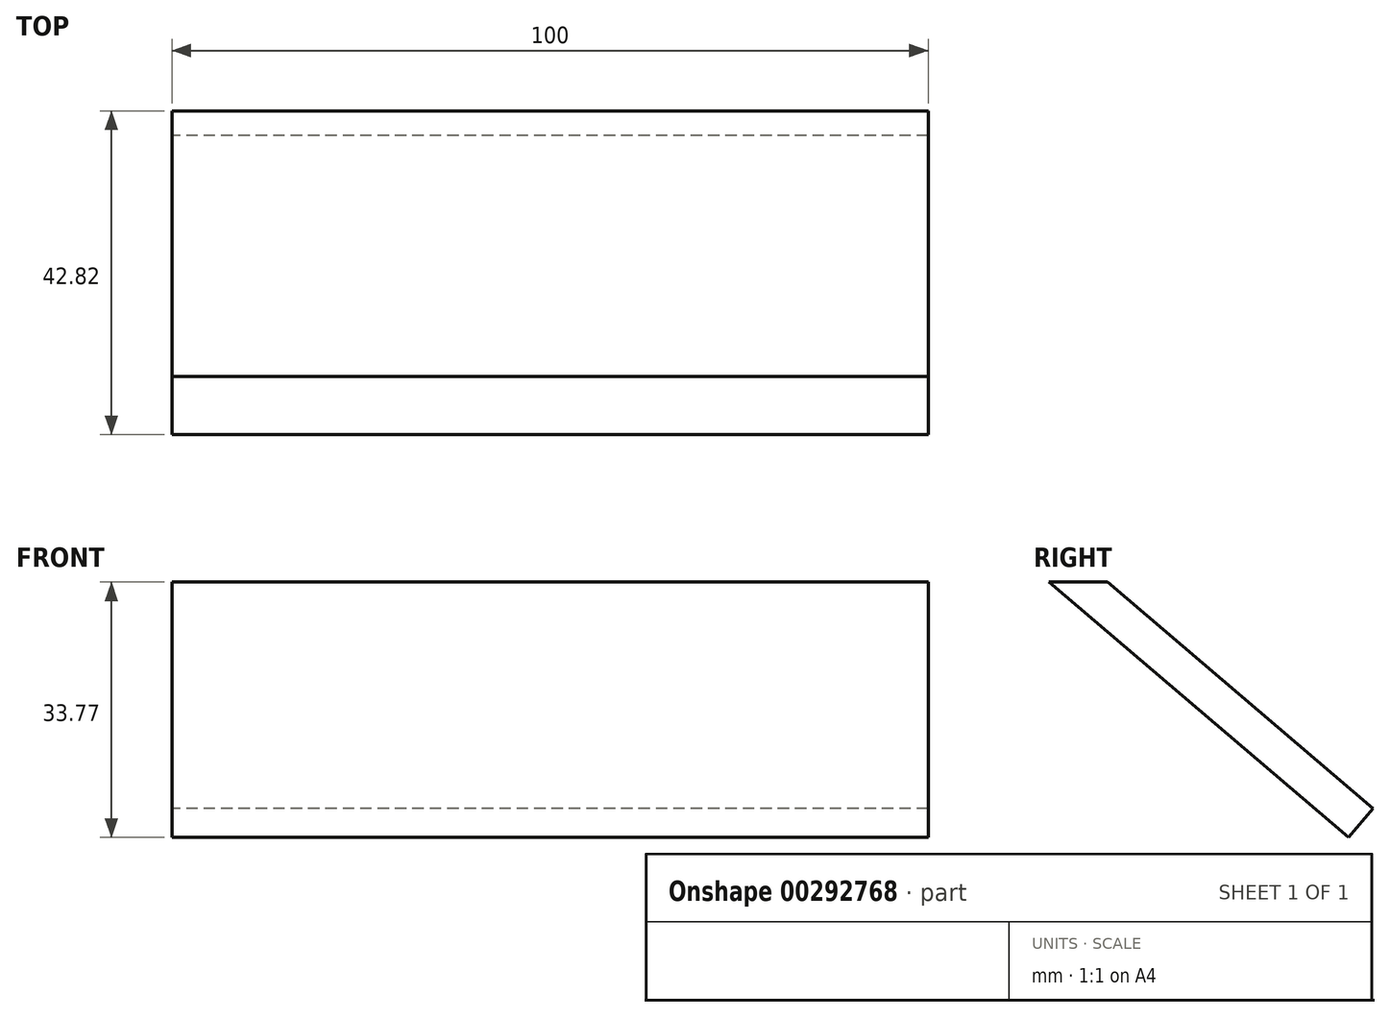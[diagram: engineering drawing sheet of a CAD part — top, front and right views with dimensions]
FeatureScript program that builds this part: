
annotation { "Feature Type Name" : "Feature", "Feature Type Description" : "" }
export const myFeature = defineFeature(function(context is Context, id is Id, definition is map)
    precondition{}
    {
        {
            var Q0;
            Q0=qCreatedBy(makeId("Right.planeOp"),FACE);
            var sketch = newSketch(context, id + "F0", { "sketchPlane" : qUnion([Q0])});
            skLineSegment(sketch, "E0", {"start": v(-15.34, 29) * mm, "end": v(-7.64, 29) * mm});
            skLineSegment(sketch, "E1", {"start": v(-7.64, 29) * mm, "end": v(27.48, -0.97) * mm});
            skLineSegment(sketch, "E2", {"start": v(27.48, -0.97) * mm, "end": v(24.24, -4.77) * mm});
            skLineSegment(sketch, "E3", {"start": v(24.24, -4.77) * mm, "end": v(-15.34, 29) * mm});
            skSolve(sketch);
        }
        {
            var Q0;
            Q0=makeQuery(id+"F0.imprint","IMPRINT",FACE,{"disambiguationData":[TD([[makeQuery(id+"F0.imprint","IMPRINT",EDGE,{"derivedFrom":sQuery(id+"F0.wireOp",EDGE,"E0")}),-1.0]])]});
            extrude(context, id + "F1", {"entities" : qUnion([Q0]), "depth" : 100 * mm});
        }
    });
